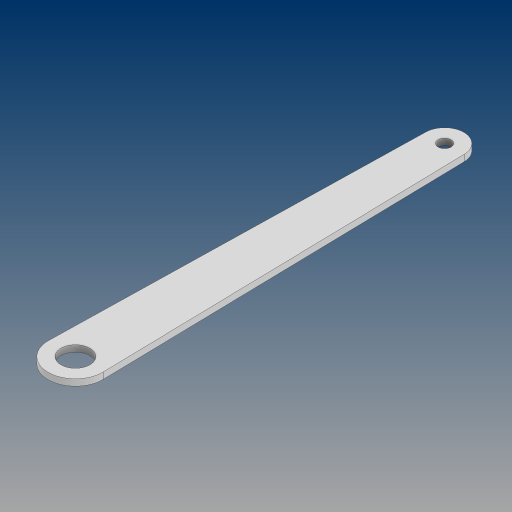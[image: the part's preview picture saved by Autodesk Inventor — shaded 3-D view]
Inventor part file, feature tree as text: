
AUTODESK INVENTOR PART (.ipt)
format: ipt  version: 2024.3 (Build 283343000, 343)  size: 95,744 bytes
history: native  units: in
note: dims shown in document units (in); Inventor stores cm internally (conversion verified against a paired STEP export)
features: extrude x1, sketch x1
ambient origin geometry x8: Origin, YZ Plane, XZ Plane, XY Plane, X Axis, Y Axis, Z Axis, Center Point
bodies: Solid1 (feature_tree)
feature tree (2):
  extrude  "Extrusion1"  Depth=0.25in
  sketch  "Sketch1"  dims[d0=14.4in d1=0.5in d2=1.125in d3=0.5in d4=0.5in d5=0.25in d6=0.0in]
